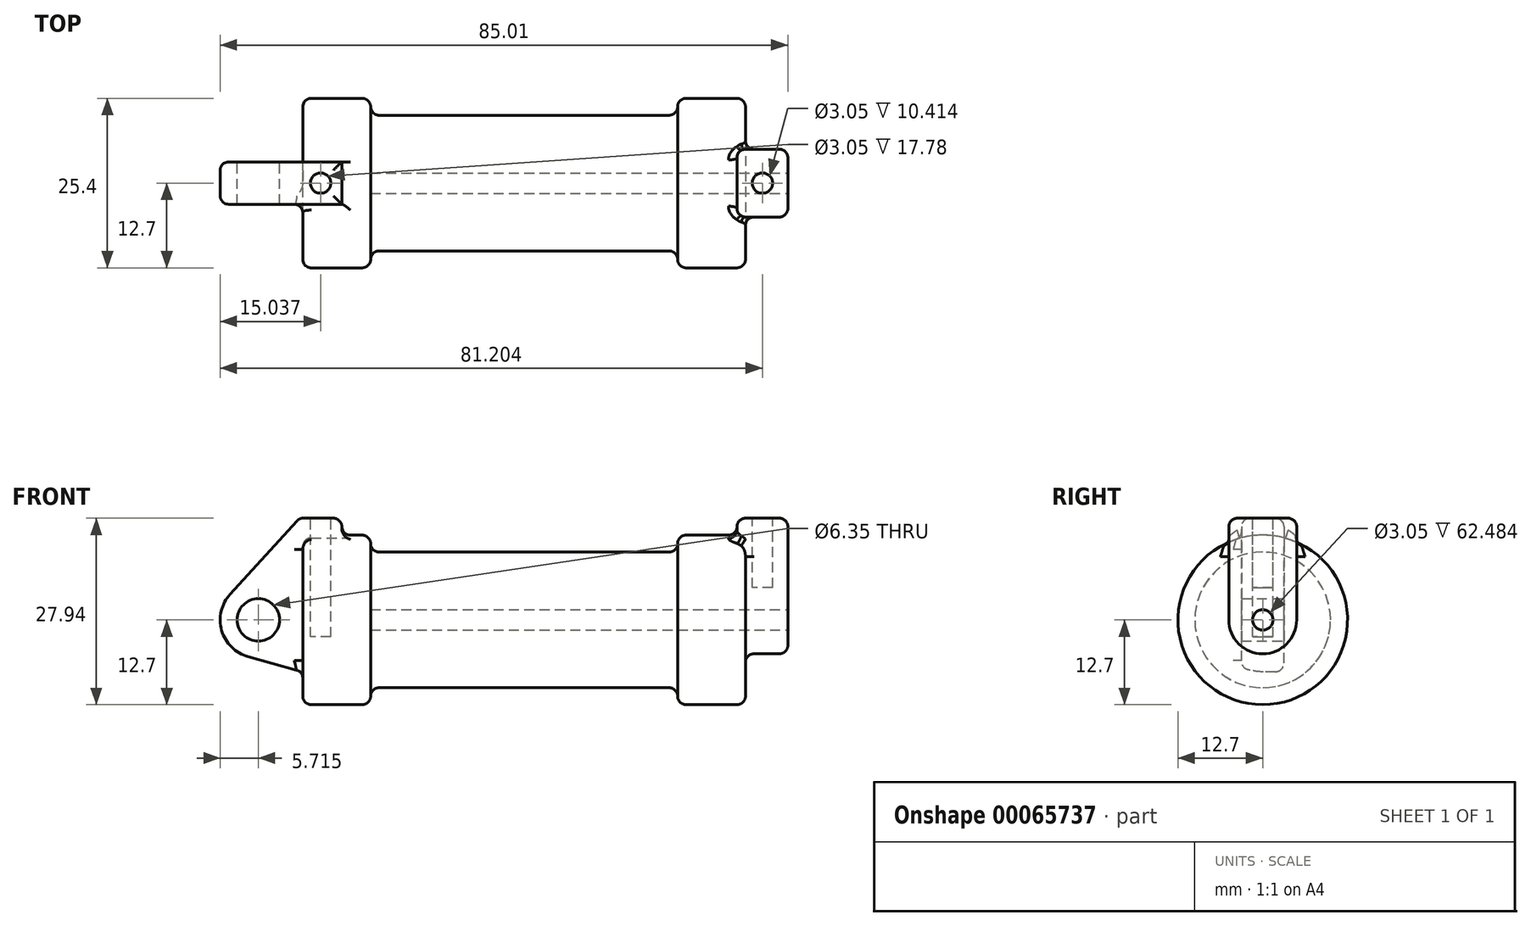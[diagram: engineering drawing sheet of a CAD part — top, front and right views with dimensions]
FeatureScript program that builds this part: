
annotation { "Feature Type Name" : "Feature", "Feature Type Description" : "" }
export const myFeature = defineFeature(function(context is Context, id is Id, definition is map)
    precondition{}
    {
        {
            var Q0;
            Q0=qCreatedBy(makeId("Front.planeOp"),FACE);
            var sketch = newSketch(context, id + "F0", { "sketchPlane" : qUnion([Q0])});
            skLineSegment(sketch, "E0", {"start": v(0, 0) * mm, "end": v(0, 12.7) * mm});
            skLineSegment(sketch, "E1", {"start": v(0, 12.7) * mm, "end": v(10.16, 12.7) * mm});
            skLineSegment(sketch, "E2", {"start": v(10.16, 12.7) * mm, "end": v(10.16, 10.16) * mm});
            skLineSegment(sketch, "E3", {"start": v(10.16, 10.16) * mm, "end": v(56.13, 10.16) * mm});
            skLineSegment(sketch, "E4", {"start": v(56.13, 10.16) * mm, "end": v(56.13, 12.7) * mm});
            skLineSegment(sketch, "E5", {"start": v(56.13, 12.7) * mm, "end": v(66.3, 12.7) * mm});
            skLineSegment(sketch, "E6", {"start": v(66.3, 12.7) * mm, "end": v(66.3, 0) * mm});
            skLineSegment(sketch, "E7", {"start": v(66.3, 0) * mm, "end": v(0, 0) * mm});
            skLineSegment(sketch, "E8", {"start": v(5.84, 15.24) * mm, "end": v(-0.5, 15.24) * mm});
            skLineSegment(sketch, "E9", {"start": v(-0.5, 15.24) * mm, "end": v(-10.88, 3.85) * mm});
            skLineSegment(sketch, "E10", {"start": v(0, 0) * mm, "end": v(-6.65, 0) * mm});
            skCircle(sketch, "E11", {"center": v(-6.65, 0) * mm, "radius": 5.72 * mm});
            skCircle(sketch, "E12", {"center": v(-6.65, 0) * mm, "radius": 3.18 * mm});
            skLineSegment(sketch, "E13", {"start": v(5.84, 15.24) * mm, "end": v(5.84, -9.4) * mm});
            skLineSegment(sketch, "E14", {"start": v(5.84, -9.4) * mm, "end": v(-8.18, -5.5) * mm});
            skSolve(sketch);
        }
        {
            var Q0;
            {var subQ3=sQuery(id+"F0.wireOp",EDGE,"E0");Q0=makeQuery(id+"F0.imprint","IMPRINT",FACE,{"disambiguationData":[TD([[makeQuery(id+"F0.imprint","IMPRINT",EDGE,{"derivedFrom":subQ3}),1.0]])]});}
            var Q1;
            {var subQ4=sQuery(id+"F0.wireOp",EDGE,"E12");Q1=makeQuery(id+"F0.imprint","IMPRINT",FACE,{"disambiguationData":[TD([[makeQuery(id+"F0.imprint","IMPRINT",EDGE,{"derivedFrom":subQ4}),-1.0]])]});}
            var Q2;
            {var subQ0=sQuery(id+"F0.wireOp",EDGE,"E14");Q2=makeQuery(id+"F0.imprint","IMPRINT",FACE,{"disambiguationData":[TD([[makeQuery(id+"F0.imprint","IMPRINT",EDGE,{"derivedFrom":subQ0}),-1.0]])]});}
            var Q3;
            {var subQ0=sQuery(id+"F0.wireOp",EDGE,"E0");Q3=makeQuery(id+"F0.imprint","IMPRINT",FACE,{"disambiguationData":[TD([[makeQuery(id+"F0.imprint","IMPRINT",EDGE,{"derivedFrom":subQ0}),-1.0]])]});}
            extrude(context, id + "F1", {"entities" : qUnion([Q0, Q1, Q2, Q3]), "endBound" : BoundingType.SYMMETRIC, "depth" : 6.35 * mm});
        }
        {
            var Q0;
            {var subQ0=sQuery(id+"F0.wireOp",EDGE,"E0");Q0=makeQuery(id+"F0.imprint","IMPRINT",FACE,{"disambiguationData":[TD([[makeQuery(id+"F0.imprint","IMPRINT",EDGE,{"derivedFrom":subQ0}),-1.0]])]});}
            var Q1;
            {var subQ0=sQuery(id+"F0.wireOp",EDGE,"E2");Q1=makeQuery(id+"F0.imprint","IMPRINT",FACE,{"disambiguationData":[TD([[makeQuery(id+"F0.imprint","IMPRINT",EDGE,{"derivedFrom":subQ0}),-1.0]])]});}
            var Q2;
            Q2=sQuery(id+"F0.wireOp",EDGE,"E7");
            revolve(context, id + "F2", {"operationType" : NewBodyOperationType.ADD, "entities" : qUnion([Q0, Q1]), "axis" : qUnion([Q2]), "revolveType" : RevolveType.FULL});
        }
        {
            var Q0;
            Q0=makeQuery(id+"F2.opRevolve","SWEPT_FACE",FACE,{"disambiguationData":[OSD([sQuery(id+"F0.wireOp",EDGE,"E6")])]});
            var sketch = newSketch(context, id + "F3", { "sketchPlane" : qUnion([Q0])});
            skCircle(sketch, "E15", {"center": v(0, 0) * mm, "radius": 1.52 * mm});
            skCircle(sketch, "E16", {"center": v(0, 0) * mm, "radius": 5.08 * mm});
            skLineSegment(sketch, "E17", {"start": v(-5.08, 0) * mm, "end": v(-5.08, 15.24) * mm});
            skLineSegment(sketch, "E18", {"start": v(5.08, 0) * mm, "end": v(5.08, 15.24) * mm});
            skLineSegment(sketch, "E19", {"start": v(-5.08, 15.24) * mm, "end": v(5.08, 15.24) * mm});
            skSolve(sketch);
        }
        {
            var Q0;
            {var subQ0=sQuery(id+"F3.wireOp",EDGE,"E19");Q0=makeQuery(id+"F3.imprint","IMPRINT",FACE,{"disambiguationData":[TD([[makeQuery(id+"F3.imprint","IMPRINT",EDGE,{"derivedFrom":subQ0}),-1.0]])]});}
            var Q1;
            {var subQ0=sQuery(id+"F3.wireOp",EDGE,"E17");var subQ1=sQuery(id+"F3.wireOp",EDGE,"E16");var subQ2=makeQuery(id+"F3.imprint","INTERSECT",VERTEX,{"derivedFrom":[subQ1,subQ0]});Q1=makeQuery(id+"F3.imprint","IMPRINT",FACE,{"disambiguationData":[TD([[makeQuery(id+"F3.imprint","IMPRINT",EDGE,{"disambiguationData":[TD([[subQ2,1.0]])],"derivedFrom":subQ1}),-1.0]])]});}
            var Q2;
            Q2=makeQuery(id+"F3.imprint","IMPRINT",FACE,{"disambiguationData":[TD([[makeQuery(id+"F3.imprint","IMPRINT",EDGE,{"derivedFrom":sQuery(id+"F3.wireOp",EDGE,"E15")}),-1.0]])]});
            extrude(context, id + "F4", {"entities" : qUnion([Q0, Q1, Q2]), "operationType" : NewBodyOperationType.ADD, "oppositeDirection" : true, "depth" : 1.27 * mm, "hasSecondDirection" : true, "secondDirectionOppositeDirection" : false, "secondDirectionDepth" : 6.35 * mm});
        }
        {
            var Q0;
            Q0=makeQuery(id+"F4.boolean.opBoolean","SPLIT",FACE,{"disambiguationData":[TD([makeQuery(id+"F4.opExtrude","SWEPT_FACE",FACE,{"disambiguationData":[OSD([sQuery(id+"F3.wireOp",EDGE,"E15")])]})])],"derivedFrom":makeQuery(id+"F2.opRevolve","SWEPT_FACE",FACE,{"disambiguationData":[OSD([sQuery(id+"F0.wireOp",EDGE,"E6")])]})});
            var Q1;
            Q1=makeQuery(id+"F2.opRevolve","SWEPT_FACE",FACE,{"disambiguationData":[OSD([sQuery(id+"F0.wireOp",EDGE,"E2")])]});
            extrude(context, id + "F5", {"entities" : qUnion([Q0]), "operationType" : NewBodyOperationType.REMOVE, "endBound" : BoundingType.UP_TO_SURFACE, "oppositeDirection" : true, "endBoundEntityFace" : qUnion([Q1]), "depth" : 25.4 * mm});
        }
        {
            var Q0;
            Q0=makeQuery(id+"F4.opExtrude","SWEPT_FACE",FACE,{"disambiguationData":[OSD([sQuery(id+"F3.wireOp",EDGE,"E19")])]});
            var sketch = newSketch(context, id + "F6", { "sketchPlane" : qUnion([Q0])});
            skCircle(sketch, "E20", {"center": v(68.83, 0) * mm, "radius": 1.52 * mm});
            skPoint(sketch, "E20.centerSnap0", {"position": v(65.02, 0) * mm});
            skPoint(sketch, "E20.centerSnap1", {"position": v(68.83, 5.08) * mm});
            skCircle(sketch, "E21", {"center": v(2.67, 0) * mm, "radius": 1.52 * mm});
            skPoint(sketch, "E21.centerSnap0", {"position": v(5.84, 0) * mm});
            skPoint(sketch, "E21.centerSnap1", {"position": v(2.67, 3.18) * mm});
            skSolve(sketch);
        }
        {
            var Q0;
            Q0=makeQuery(id+"F6.imprint","IMPRINT",FACE,{"disambiguationData":[TD([[makeQuery(id+"F6.imprint","IMPRINT",EDGE,{"derivedFrom":sQuery(id+"F6.wireOp",EDGE,"E20")}),1.0]])]});
            extrude(context, id + "F7", {"entities" : qUnion([Q0]), "operationType" : NewBodyOperationType.REMOVE, "oppositeDirection" : true, "depth" : 10.4 * mm});
        }
        {
            var Q0;
            Q0=makeQuery(id+"F6.imprint","IMPRINT",FACE,{"disambiguationData":[TD([[makeQuery(id+"F6.imprint","IMPRINT",EDGE,{"derivedFrom":sQuery(id+"F6.wireOp",EDGE,"E21")}),1.0]])]});
            extrude(context, id + "F8", {"entities" : qUnion([Q0]), "operationType" : NewBodyOperationType.REMOVE, "oppositeDirection" : true, "depth" : 17.78 * mm});
        }
        {
            var Q0;
            Q0=makeQuery(id+"F2.opRevolve","SWEPT_FACE",FACE,{"disambiguationData":[OSD([sQuery(id+"F0.wireOp",EDGE,"E3")])]});
            var Q1;
            Q1=makeQuery(id+"F2.opRevolve","SWEPT_EDGE",EDGE,{"disambiguationData":[OSD([sQuery(id+"F0.wireOp",EDGE,"E1"),sQuery(id+"F0.wireOp",EDGE,"E2")])]});
            var Q2;
            Q2=makeQuery(id+"F2.opRevolve","SWEPT_EDGE",EDGE,{"disambiguationData":[OSD([sQuery(id+"F0.wireOp",EDGE,"E0"),sQuery(id+"F0.wireOp",EDGE,"E1")])]});
            var Q3;
            Q3=makeQuery(id+"F2.opRevolve","SWEPT_EDGE",EDGE,{"disambiguationData":[OSD([sQuery(id+"F0.wireOp",EDGE,"E4"),sQuery(id+"F0.wireOp",EDGE,"E5")])]});
            var Q4;
            Q4=makeQuery(id+"F2.opRevolve","SWEPT_EDGE",EDGE,{"disambiguationData":[OSD([sQuery(id+"F0.wireOp",EDGE,"E5"),sQuery(id+"F0.wireOp",EDGE,"E6")])]});
            fillet(context, id + "F9", {"entities" : qUnion([Q0, Q1, Q2, Q3, Q4]), "radius" : 1.27 * mm, "tangentPropagation" : true, "allowEdgeOverflow" : false});
        }
        {
            var Q0;
            Q0=makeQuery(id+"F1.opExtrude","SWEPT_EDGE",EDGE,{"disambiguationData":[OSD([sQuery(id+"F0.wireOp",EDGE,"E8"),sQuery(id+"F0.wireOp",EDGE,"E9")])]});
            var Q1;
            Q1=makeQuery(id+"F1.opExtrude","CAP_EDGE",EDGE,{"disambiguationData":[OSD([sQuery(id+"F0.wireOp",EDGE,"E8")])],"isStart":true});
            var Q2;
            Q2=makeQuery(id+"F1.opExtrude","CAP_EDGE",EDGE,{"disambiguationData":[OSD([sQuery(id+"F0.wireOp",EDGE,"E8")])],"isStart":false});
            var Q3;
            Q3=makeQuery(id+"F1.opExtrude","SWEPT_EDGE",EDGE,{"disambiguationData":[OSD([sQuery(id+"F0.wireOp",EDGE,"E8"),sQuery(id+"F0.wireOp",EDGE,"E13")])]});
            var Q4;
            Q4=makeQuery(id+"F1.opExtrude","SWEPT_FACE",FACE,{"disambiguationData":[OSD([sQuery(id+"F0.wireOp",EDGE,"E9")])]});
            var Q5;
            Q5=makeQuery(id+"F2.boolean.opBoolean","INTERSECT",EDGE,{"derivedFrom":[makeQuery(id+"F1.opExtrude","CAP_FACE",FACE,{"disambiguationData":[OSD([sQuery(id+"F0.wireOp",EDGE,"E8"),sQuery(id+"F0.wireOp",EDGE,"E9"),sQuery(id+"F0.wireOp",EDGE,"E11"),sQuery(id+"F0.wireOp",EDGE,"E12"),sQuery(id+"F0.wireOp",EDGE,"E13"),sQuery(id+"F0.wireOp",EDGE,"E14")])],"isStart":false}),makeQuery(id+"F2.opRevolve","SWEPT_FACE",FACE,{"disambiguationData":[OSD([sQuery(id+"F0.wireOp",EDGE,"E0")])]})]});
            var Q6;
            Q6=makeQuery(id+"F2.boolean.opBoolean","INTERSECT",EDGE,{"derivedFrom":[makeQuery(id+"F1.opExtrude","SWEPT_FACE",FACE,{"disambiguationData":[OSD([sQuery(id+"F0.wireOp",EDGE,"E13")])]}),makeQuery(id+"F2.opRevolve","SWEPT_FACE",FACE,{"disambiguationData":[OSD([sQuery(id+"F0.wireOp",EDGE,"E1")])]})]});
            fillet(context, id + "F10", {"entities" : qUnion([Q0, Q1, Q2, Q3, Q4, Q5, Q6]), "radius" : 1.27 * mm, "tangentPropagation" : true, "allowEdgeOverflow" : false});
        }
        {
            var Q0;
            Q0=makeQuery(id+"F4.opExtrude","SWEPT_FACE",FACE,{"disambiguationData":[OSD([sQuery(id+"F3.wireOp",EDGE,"E16")])]});
            var Q1;
            Q1=makeQuery(id+"F4.opExtrude","CAP_FACE",FACE,{"disambiguationData":[OSD([sQuery(id+"F3.wireOp",EDGE,"E15"),sQuery(id+"F3.wireOp",EDGE,"E16"),sQuery(id+"F3.wireOp",EDGE,"E17"),sQuery(id+"F3.wireOp",EDGE,"E18"),sQuery(id+"F3.wireOp",EDGE,"E19")])],"isStart":false});
            var Q2;
            Q2=makeQuery(id+"F4.opExtrude","SWEPT_EDGE",EDGE,{"disambiguationData":[OSD([sQuery(id+"F3.wireOp",EDGE,"E17"),sQuery(id+"F3.wireOp",EDGE,"E19")])]});
            var Q3;
            Q3=makeQuery(id+"F4.opExtrude","CAP_EDGE",EDGE,{"disambiguationData":[OSD([sQuery(id+"F3.wireOp",EDGE,"E19")])],"isStart":true});
            var Q4;
            Q4=makeQuery(id+"F4.opExtrude","SWEPT_EDGE",EDGE,{"disambiguationData":[OSD([sQuery(id+"F3.wireOp",EDGE,"E18"),sQuery(id+"F3.wireOp",EDGE,"E19")])]});
            fillet(context, id + "F11", {"entities" : qUnion([Q0, Q1, Q2, Q3, Q4]), "radius" : 1.27 * mm, "tangentPropagation" : true, "allowEdgeOverflow" : false});
        }
    });
